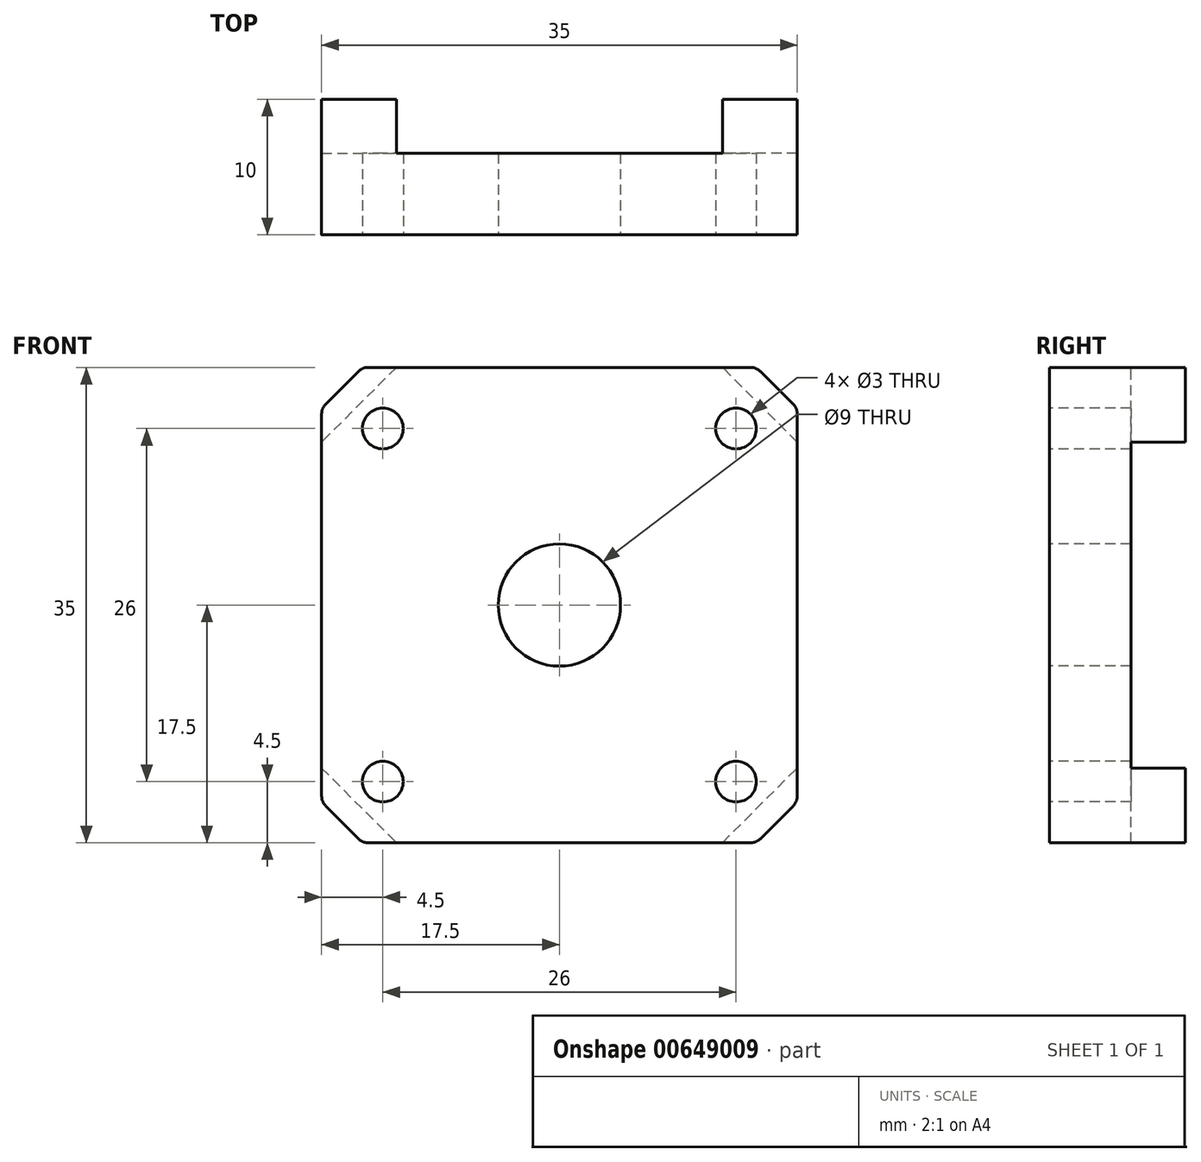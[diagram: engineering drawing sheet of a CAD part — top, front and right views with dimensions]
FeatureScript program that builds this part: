
annotation { "Feature Type Name" : "Feature", "Feature Type Description" : "" }
export const myFeature = defineFeature(function(context is Context, id is Id, definition is map)
    precondition{}
    {
        {
            var Q0;
            Q0=qCreatedBy(makeId("Front.planeOp"),FACE);
            var sketch = newSketch(context, id + "F0", { "sketchPlane" : qUnion([Q0])});
            skLineSegment(sketch, "E0.bottom", {"start": v(-17.5, 17.5) * mm, "end": v(17.5, 17.5) * mm});
            skLineSegment(sketch, "E0.top", {"start": v(-17.5, -17.5) * mm, "end": v(17.5, -17.5) * mm});
            skLineSegment(sketch, "E0.left", {"start": v(-17.5, 17.5) * mm, "end": v(-17.5, -17.5) * mm});
            skLineSegment(sketch, "E0.right", {"start": v(17.5, 17.5) * mm, "end": v(17.5, -17.5) * mm});
            skPoint(sketch, "E0.middle", {"position": v(0, 0) * mm});
            skSolve(sketch);
        }
        {
            var Q0;
            Q0=makeQuery(id+"F0.imprint","IMPRINT",FACE,{"disambiguationData":[TD([[makeQuery(id+"F0.imprint","IMPRINT",EDGE,{"derivedFrom":sQuery(id+"F0.wireOp",EDGE,"E0.bottom")}),-1.0]])]});
            extrude(context, id + "F1", {"entities" : qUnion([Q0]), "depth" : 10 * mm, "offsetDistance" : 25 * mm});
        }
        {
            var Q0;
            Q0=makeQuery(id+"F1.opExtrude","SWEPT_EDGE",EDGE,{"disambiguationData":[OSD([sQuery(id+"F0.wireOp",EDGE,"E0.bottom"),sQuery(id+"F0.wireOp",EDGE,"E0.left")])]});
            var Q1;
            Q1=makeQuery(id+"F1.opExtrude","SWEPT_EDGE",EDGE,{"disambiguationData":[OSD([sQuery(id+"F0.wireOp",EDGE,"E0.bottom"),sQuery(id+"F0.wireOp",EDGE,"E0.right")])]});
            var Q2;
            Q2=makeQuery(id+"F1.opExtrude","SWEPT_EDGE",EDGE,{"disambiguationData":[OSD([sQuery(id+"F0.wireOp",EDGE,"E0.top"),sQuery(id+"F0.wireOp",EDGE,"E0.right")])]});
            var Q3;
            Q3=makeQuery(id+"F1.opExtrude","SWEPT_EDGE",EDGE,{"disambiguationData":[OSD([sQuery(id+"F0.wireOp",EDGE,"E0.top"),sQuery(id+"F0.wireOp",EDGE,"E0.left")])]});
            chamfer(context, id + "F2", {"entities" : qUnion([Q0, Q1, Q2, Q3]), "width" : 3 * mm, "tangentPropagation" : true});
        }
        {
            var Q0;
            {var subQ0=sQuery(id+"F0.wireOp",EDGE,"E0.bottom");Q0=makeQuery(id+"F2.opChamfer","BLEND_EDGE",EDGE,{"blendedFrom":[makeQuery(id+"F1.opExtrude","SWEPT_EDGE",EDGE,{"disambiguationData":[OSD([subQ0,sQuery(id+"F0.wireOp",EDGE,"E0.left")])]}),makeQuery(id+"F1.opExtrude","SWEPT_FACE",FACE,{"disambiguationData":[OSD([subQ0])]})],"blendedInto":[makeQuery(id+"F1.opExtrude","SWEPT_FACE",FACE,{"disambiguationData":[OSD([subQ0])]})]});}
            var Q1;
            {var subQ0=sQuery(id+"F0.wireOp",EDGE,"E0.bottom");Q1=makeQuery(id+"F2.opChamfer","BLEND_EDGE",EDGE,{"blendedFrom":[makeQuery(id+"F1.opExtrude","SWEPT_EDGE",EDGE,{"disambiguationData":[OSD([subQ0,sQuery(id+"F0.wireOp",EDGE,"E0.right")])]}),makeQuery(id+"F1.opExtrude","SWEPT_FACE",FACE,{"disambiguationData":[OSD([subQ0])]})],"blendedInto":[makeQuery(id+"F1.opExtrude","SWEPT_FACE",FACE,{"disambiguationData":[OSD([subQ0])]})]});}
            var Q2;
            {var subQ0=sQuery(id+"F0.wireOp",EDGE,"E0.right");Q2=makeQuery(id+"F2.opChamfer","BLEND_EDGE",EDGE,{"blendedFrom":[makeQuery(id+"F1.opExtrude","SWEPT_EDGE",EDGE,{"disambiguationData":[OSD([sQuery(id+"F0.wireOp",EDGE,"E0.bottom"),subQ0])]}),makeQuery(id+"F1.opExtrude","SWEPT_FACE",FACE,{"disambiguationData":[OSD([subQ0])]})],"blendedInto":[makeQuery(id+"F1.opExtrude","SWEPT_FACE",FACE,{"disambiguationData":[OSD([subQ0])]})]});}
            var Q3;
            {var subQ0=sQuery(id+"F0.wireOp",EDGE,"E0.right");Q3=makeQuery(id+"F2.opChamfer","BLEND_EDGE",EDGE,{"blendedFrom":[makeQuery(id+"F1.opExtrude","SWEPT_EDGE",EDGE,{"disambiguationData":[OSD([sQuery(id+"F0.wireOp",EDGE,"E0.top"),subQ0])]}),makeQuery(id+"F1.opExtrude","SWEPT_FACE",FACE,{"disambiguationData":[OSD([subQ0])]})],"blendedInto":[makeQuery(id+"F1.opExtrude","SWEPT_FACE",FACE,{"disambiguationData":[OSD([subQ0])]})]});}
            var Q4;
            {var subQ0=sQuery(id+"F0.wireOp",EDGE,"E0.top");Q4=makeQuery(id+"F2.opChamfer","BLEND_EDGE",EDGE,{"blendedFrom":[makeQuery(id+"F1.opExtrude","SWEPT_EDGE",EDGE,{"disambiguationData":[OSD([subQ0,sQuery(id+"F0.wireOp",EDGE,"E0.right")])]}),makeQuery(id+"F1.opExtrude","SWEPT_FACE",FACE,{"disambiguationData":[OSD([subQ0])]})],"blendedInto":[makeQuery(id+"F1.opExtrude","SWEPT_FACE",FACE,{"disambiguationData":[OSD([subQ0])]})]});}
            var Q5;
            {var subQ0=sQuery(id+"F0.wireOp",EDGE,"E0.top");Q5=makeQuery(id+"F2.opChamfer","BLEND_EDGE",EDGE,{"blendedFrom":[makeQuery(id+"F1.opExtrude","SWEPT_EDGE",EDGE,{"disambiguationData":[OSD([subQ0,sQuery(id+"F0.wireOp",EDGE,"E0.left")])]}),makeQuery(id+"F1.opExtrude","SWEPT_FACE",FACE,{"disambiguationData":[OSD([subQ0])]})],"blendedInto":[makeQuery(id+"F1.opExtrude","SWEPT_FACE",FACE,{"disambiguationData":[OSD([subQ0])]})]});}
            var Q6;
            {var subQ0=sQuery(id+"F0.wireOp",EDGE,"E0.left");Q6=makeQuery(id+"F2.opChamfer","BLEND_EDGE",EDGE,{"blendedFrom":[makeQuery(id+"F1.opExtrude","SWEPT_EDGE",EDGE,{"disambiguationData":[OSD([sQuery(id+"F0.wireOp",EDGE,"E0.top"),subQ0])]}),makeQuery(id+"F1.opExtrude","SWEPT_FACE",FACE,{"disambiguationData":[OSD([subQ0])]})],"blendedInto":[makeQuery(id+"F1.opExtrude","SWEPT_FACE",FACE,{"disambiguationData":[OSD([subQ0])]})]});}
            var Q7;
            {var subQ0=sQuery(id+"F0.wireOp",EDGE,"E0.left");Q7=makeQuery(id+"F2.opChamfer","BLEND_EDGE",EDGE,{"blendedFrom":[makeQuery(id+"F1.opExtrude","SWEPT_EDGE",EDGE,{"disambiguationData":[OSD([sQuery(id+"F0.wireOp",EDGE,"E0.bottom"),subQ0])]}),makeQuery(id+"F1.opExtrude","SWEPT_FACE",FACE,{"disambiguationData":[OSD([subQ0])]})],"blendedInto":[makeQuery(id+"F1.opExtrude","SWEPT_FACE",FACE,{"disambiguationData":[OSD([subQ0])]})]});}
            fillet(context, id + "F3", {"entities" : qUnion([Q0, Q1, Q2, Q3, Q4, Q5, Q6, Q7]), "radius" : 1 * mm, "tangentPropagation" : true, "allowEdgeOverflow" : false});
        }
        {
            var Q0;
            Q0=makeQuery(id+"F1.opExtrude","CAP_FACE",FACE,{"disambiguationData":[OSD([sQuery(id+"F0.wireOp",EDGE,"E0.bottom"),sQuery(id+"F0.wireOp",EDGE,"E0.top"),sQuery(id+"F0.wireOp",EDGE,"E0.left"),sQuery(id+"F0.wireOp",EDGE,"E0.right")])],"isStart":false});
            var sketch = newSketch(context, id + "F4", { "sketchPlane" : qUnion([Q0])});
            skCircle(sketch, "E1", {"center": v(-13, 13) * mm, "radius": 1.5 * mm});
            skCircle(sketch, "E2.1.0", {"center": v(-13, -13) * mm, "radius": 1.5 * mm});
            skCircle(sketch, "E2.2.0", {"center": v(13, -13) * mm, "radius": 1.5 * mm});
            skCircle(sketch, "E2.3.0", {"center": v(13, 13) * mm, "radius": 1.5 * mm});
            skPoint(sketch, "E2.center", {"position": v(0, 0) * mm});
            skSolve(sketch);
        }
        {
            var Q0;
            Q0=qSketchRegion(id+"F4",true);
            extrude(context, id + "F5", {"entities" : qUnion([Q0]), "operationType" : NewBodyOperationType.REMOVE, "endBound" : BoundingType.THROUGH_ALL, "oppositeDirection" : true, "depth" : 25 * mm, "offsetDistance" : 25 * mm});
        }
        {
            var Q0;
            Q0=makeQuery(id+"F1.opExtrude","CAP_FACE",FACE,{"disambiguationData":[OSD([sQuery(id+"F0.wireOp",EDGE,"E0.bottom"),sQuery(id+"F0.wireOp",EDGE,"E0.top"),sQuery(id+"F0.wireOp",EDGE,"E0.left"),sQuery(id+"F0.wireOp",EDGE,"E0.right")])],"isStart":false});
            var sketch = newSketch(context, id + "F6", { "sketchPlane" : qUnion([Q0])});
            skCircle(sketch, "E3", {"center": v(0, 0) * mm, "radius": 4.5 * mm});
            skSolve(sketch);
        }
        {
            var Q0;
            Q0=makeQuery(id+"F6.imprint","IMPRINT",FACE,{"disambiguationData":[TD([[makeQuery(id+"F6.imprint","IMPRINT",EDGE,{"derivedFrom":sQuery(id+"F6.wireOp",EDGE,"E3")}),1.0]])]});
            extrude(context, id + "F7", {"entities" : qUnion([Q0]), "operationType" : NewBodyOperationType.REMOVE, "endBound" : BoundingType.THROUGH_ALL, "oppositeDirection" : true, "depth" : 25 * mm, "offsetDistance" : 25 * mm});
        }
        {
            var Q0;
            Q0=makeQuery(id+"F1.opExtrude","CAP_FACE",FACE,{"disambiguationData":[OSD([sQuery(id+"F0.wireOp",EDGE,"E0.bottom"),sQuery(id+"F0.wireOp",EDGE,"E0.top"),sQuery(id+"F0.wireOp",EDGE,"E0.left"),sQuery(id+"F0.wireOp",EDGE,"E0.right")])],"isStart":true});
            var sketch = newSketch(context, id + "F8", { "sketchPlane" : qUnion([Q0])});
            skLineSegment(sketch, "E4.bottom", {"start": v(-12, 17.5) * mm, "end": v(12, 17.5) * mm});
            skLineSegment(sketch, "E4.top", {"start": v(-12, -17.5) * mm, "end": v(12, -17.5) * mm});
            skLineSegment(sketch, "E4.left", {"start": v(-17.5, 12) * mm, "end": v(-17.5, -12) * mm});
            skLineSegment(sketch, "E4.right", {"start": v(17.5, 12) * mm, "end": v(17.5, -12) * mm});
            skPoint(sketch, "E4.middle", {"position": v(0, 0) * mm});
            skLineSegment(sketch, "E5", {"start": v(-17.5, 12) * mm, "end": v(-12, 17.5) * mm});
            skLineSegment(sketch, "E6.1.0", {"start": v(-12, -17.5) * mm, "end": v(-17.5, -12) * mm});
            skLineSegment(sketch, "E6.2.0", {"start": v(17.5, -12) * mm, "end": v(12, -17.5) * mm});
            skLineSegment(sketch, "E6.3.0", {"start": v(12, 17.5) * mm, "end": v(17.5, 12) * mm});
            skPoint(sketch, "E7.orphan", {"position": v(-17.5, 17.5) * mm});
            skPoint(sketch, "E8.orphan", {"position": v(-17.5, -17.5) * mm});
            skPoint(sketch, "E9.orphan", {"position": v(17.5, -17.5) * mm});
            skPoint(sketch, "E10.orphan", {"position": v(17.5, 17.5) * mm});
            skSolve(sketch);
        }
        {
            var Q0;
            Q0=qSketchRegion(id+"F8",true);
            extrude(context, id + "F9", {"entities" : qUnion([Q0]), "operationType" : NewBodyOperationType.REMOVE, "oppositeDirection" : true, "depth" : 4 * mm, "offsetDistance" : 25 * mm});
        }
    });
